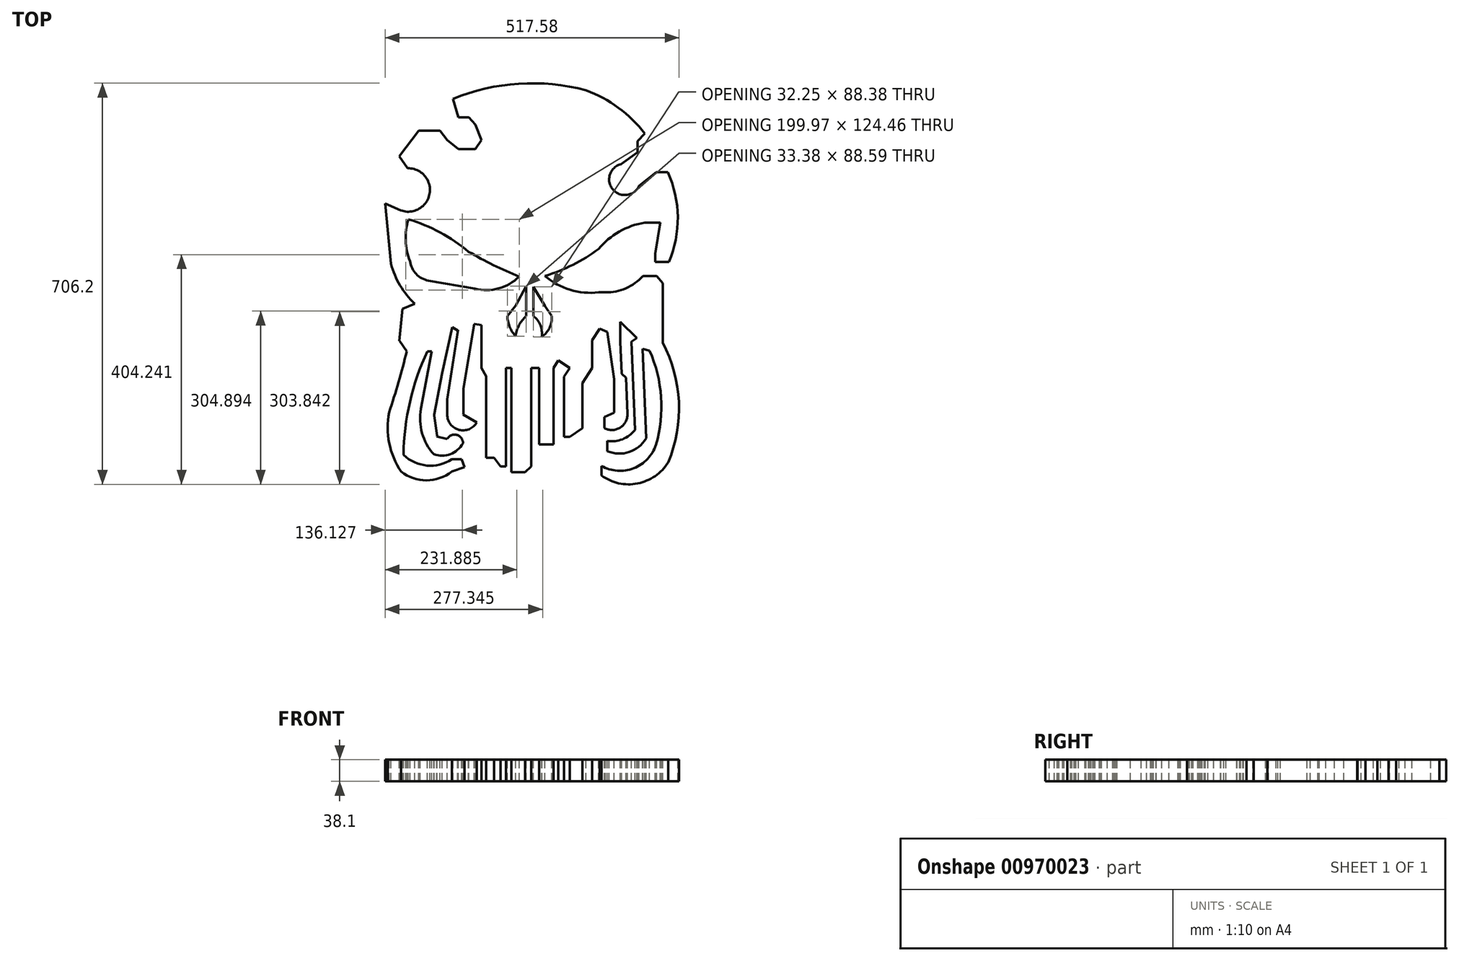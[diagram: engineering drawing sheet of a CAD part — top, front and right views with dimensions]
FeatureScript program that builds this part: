
annotation { "Feature Type Name" : "Feature", "Feature Type Description" : "" }
export const myFeature = defineFeature(function(context is Context, id is Id, definition is map)
    precondition{}
    {
        {
            var Q0;
            Q0=qCreatedBy(makeId("Top.planeOp"),FACE);
            var sketch = newSketch(context, id + "F0", { "sketchPlane" : qUnion([Q0])});
            skLineSegment(sketch, "E0", {"start": v(-722.51, 11.97) * mm, "end": v(-722.51, -131.34) * mm});
            skLineSegment(sketch, "E1", {"start": v(-722.51, -131.34) * mm, "end": v(-708.67, -131.34) * mm});
            skLineSegment(sketch, "E2", {"start": v(-708.67, -131.34) * mm, "end": v(-697.27, -146.82) * mm});
            skLineSegment(sketch, "E3", {"start": v(-697.27, -146.82) * mm, "end": v(-687.81, -146.82) * mm});
            skLineSegment(sketch, "E4", {"start": v(-687.81, -146.82) * mm, "end": v(-687.81, 12.03) * mm});
            skLineSegment(sketch, "E5", {"start": v(-687.81, 12.03) * mm, "end": v(-687.81, 26.51) * mm});
            skLineSegment(sketch, "E6", {"start": v(-687.81, 26.51) * mm, "end": v(-678.37, 26.51) * mm});
            skLineSegment(sketch, "E7", {"start": v(-678.37, 26.51) * mm, "end": v(-678.37, -157.24) * mm});
            skLineSegment(sketch, "E8", {"start": v(-678.37, -157.24) * mm, "end": v(-653.98, -157.24) * mm});
            skLineSegment(sketch, "E9", {"start": v(-653.98, -157.24) * mm, "end": v(-643.31, -146.82) * mm});
            skLineSegment(sketch, "E10", {"start": v(-643.31, -146.82) * mm, "end": v(-643.31, 26.51) * mm});
            skLineSegment(sketch, "E11", {"start": v(-643.31, 26.51) * mm, "end": v(-629.14, 26.51) * mm});
            skLineSegment(sketch, "E12", {"start": v(-629.14, 26.51) * mm, "end": v(-629.14, -107.97) * mm});
            skLineSegment(sketch, "E13", {"start": v(-629.14, -107.97) * mm, "end": v(-618.05, -107.97) * mm});
            skLineSegment(sketch, "E14", {"start": v(-618.05, -107.97) * mm, "end": v(-604.25, -107.97) * mm});
            skLineSegment(sketch, "E15", {"start": v(-604.25, -107.97) * mm, "end": v(-604.25, 26.51) * mm});
            skLineSegment(sketch, "E16", {"start": v(-604.25, 26.51) * mm, "end": v(-595.66, 39.65) * mm});
            skLineSegment(sketch, "E17", {"start": v(-595.66, 39.65) * mm, "end": v(-575.55, 26.51) * mm});
            skLineSegment(sketch, "E18", {"start": v(-575.55, 26.51) * mm, "end": v(-585.6, 11.12) * mm});
            skLineSegment(sketch, "E19", {"start": v(-585.6, 11.12) * mm, "end": v(-585.6, -94.7) * mm});
            skLineSegment(sketch, "E20", {"start": v(-585.6, -94.7) * mm, "end": v(-575.55, -94.7) * mm});
            skLineSegment(sketch, "E21", {"start": v(-575.55, -94.7) * mm, "end": v(-553.4, -79.77) * mm});
            skLineSegment(sketch, "E22", {"start": v(-553.4, -79.77) * mm, "end": v(-553.4, 0) * mm});
            skLineSegment(sketch, "E23", {"start": v(-553.4, 0) * mm, "end": v(-536.08, 26.51) * mm});
            skLineSegment(sketch, "E24", {"start": v(-536.08, 26.51) * mm, "end": v(-536.08, 75.42) * mm});
            skLineSegment(sketch, "E25", {"start": v(-536.08, 75.42) * mm, "end": v(-522.9, 95.58) * mm});
            skArc(sketch, "E26", {"start": v(-546.97, 515.55) * mm, "mid": v(-665.37, 527.1) * mm, "end": v(-781.28, 500.3) * mm});
            skArc(sketch, "E27", {"start": v(-890.2, 209.79) * mm, "mid": v(-874.31, 171.83) * mm, "end": v(-848.63, 139.69) * mm});
            skLineSegment(sketch, "E28", {"start": v(-890.2, 209.79) * mm, "end": v(-900.6, 315.97) * mm});
            skArc(sketch, "E29", {"start": v(-873.07, 303.95) * mm, "mid": v(-822.23, 333.84) * mm, "end": v(-861.1, 378.2) * mm});
            skLineSegment(sketch, "E30", {"start": v(-873.07, 303.95) * mm, "end": v(-900.6, 315.97) * mm});
            skLineSegment(sketch, "E31", {"start": v(-861.1, 378.2) * mm, "end": v(-876, 399.5) * mm});
            skLineSegment(sketch, "E32", {"start": v(-876, 399.5) * mm, "end": v(-841.26, 444.55) * mm});
            skLineSegment(sketch, "E33", {"start": v(-841.26, 444.55) * mm, "end": v(-804.24, 444.55) * mm});
            skLineSegment(sketch, "E34", {"start": v(-804.24, 444.55) * mm, "end": v(-791.29, 428) * mm});
            skLineSegment(sketch, "E35", {"start": v(-791.29, 428) * mm, "end": v(-771.63, 412.14) * mm});
            skLineSegment(sketch, "E36", {"start": v(-771.63, 412.14) * mm, "end": v(-742.1, 412.14) * mm});
            skLineSegment(sketch, "E37", {"start": v(-742.1, 412.14) * mm, "end": v(-731.04, 428) * mm});
            skLineSegment(sketch, "E38", {"start": v(-731.04, 428) * mm, "end": v(-742.1, 455.33) * mm});
            skLineSegment(sketch, "E39", {"start": v(-742.1, 455.33) * mm, "end": v(-753.4, 467.53) * mm});
            skLineSegment(sketch, "E40", {"start": v(-753.4, 467.53) * mm, "end": v(-771.63, 467.53) * mm});
            skLineSegment(sketch, "E41", {"start": v(-771.63, 467.53) * mm, "end": v(-781.28, 500.3) * mm});
            skArc(sketch, "E42", {"start": v(-443.19, 439.34) * mm, "mid": v(-489.8, 484.64) * mm, "end": v(-546.97, 515.55) * mm});
            skLineSegment(sketch, "E43", {"start": v(-443.19, 439.34) * mm, "end": v(-455.81, 426.16) * mm});
            skLineSegment(sketch, "E44", {"start": v(-455.81, 426.16) * mm, "end": v(-455.81, 406.54) * mm});
            skLineSegment(sketch, "E45", {"start": v(-455.81, 406.54) * mm, "end": v(-485.44, 385.35) * mm});
            skArc(sketch, "E46", {"start": v(-485.44, 385.35) * mm, "mid": v(-499.49, 340.79) * mm, "end": v(-453.23, 347.45) * mm});
            skLineSegment(sketch, "E47", {"start": v(-453.23, 347.45) * mm, "end": v(-423.25, 371.41) * mm});
            skLineSegment(sketch, "E48", {"start": v(-423.25, 371.41) * mm, "end": v(-402.75, 371.1) * mm});
            skArc(sketch, "E49", {"start": v(-400.77, 213.04) * mm, "mid": v(-385.19, 292.28) * mm, "end": v(-402.75, 371.1) * mm});
            skLineSegment(sketch, "E50", {"start": v(-400.77, 213.04) * mm, "end": v(-424.77, 213.04) * mm});
            skLineSegment(sketch, "E51", {"start": v(-424.77, 213.04) * mm, "end": v(-424.77, 227.84) * mm});
            skLineSegment(sketch, "E52", {"start": v(-424.77, 227.84) * mm, "end": v(-415.97, 282.48) * mm});
            skArc(sketch, "E53", {"start": v(-443.19, 282.48) * mm, "mid": v(-488.23, 266.6) * mm, "end": v(-524.75, 235.83) * mm});
            skLineSegment(sketch, "E54", {"start": v(-443.19, 282.48) * mm, "end": v(-415.97, 282.48) * mm});
            skArc(sketch, "E55", {"start": v(-618.96, 188.64) * mm, "mid": v(-569.87, 208.28) * mm, "end": v(-524.75, 235.83) * mm});
            skArc(sketch, "E56", {"start": v(-618.96, 188.64) * mm, "mid": v(-574.9, 164.26) * mm, "end": v(-524.75, 159.64) * mm});
            skArc(sketch, "E57", {"start": v(-512.7, 159.64) * mm, "mid": v(-476.43, 166.9) * mm, "end": v(-446.5, 188.64) * mm});
            skLineSegment(sketch, "E58", {"start": v(-512.7, 159.64) * mm, "end": v(-524.75, 159.64) * mm});
            skLineSegment(sketch, "E59", {"start": v(-446.5, 188.64) * mm, "end": v(-422.22, 188.64) * mm});
            skLineSegment(sketch, "E60", {"start": v(-422.22, 188.64) * mm, "end": v(-411.7, 176) * mm});
            skLineSegment(sketch, "E61", {"start": v(-411.7, 176) * mm, "end": v(-411.7, 128.35) * mm});
            skLineSegment(sketch, "E62", {"start": v(-411.7, 128.35) * mm, "end": v(-411.7, 104.7) * mm});
            skLineSegment(sketch, "E63", {"start": v(-411.7, 104.7) * mm, "end": v(-411.7, 71.28) * mm});
            skArc(sketch, "E64", {"start": v(-402.15, -139.77) * mm, "mid": v(-383.27, -33.18) * mm, "end": v(-411.7, 71.28) * mm});
            skArc(sketch, "E65", {"start": v(-519.79, -162.6) * mm, "mid": v(-455.99, -176.83) * mm, "end": v(-402.15, -139.77) * mm});
            skLineSegment(sketch, "E66", {"start": v(-519.79, -162.6) * mm, "end": v(-519.79, -145.96) * mm});
            skArc(sketch, "E67", {"start": v(-519.79, -145.96) * mm, "mid": v(-462.8, -149.95) * mm, "end": v(-423.38, -108.6) * mm});
            skArc(sketch, "E68", {"start": v(-423.38, -108.6) * mm, "mid": v(-414.63, -24.65) * mm, "end": v(-434.9, 57.3) * mm});
            skLineSegment(sketch, "E69", {"start": v(-434.9, 57.3) * mm, "end": v(-446.95, 59.87) * mm});
            skLineSegment(sketch, "E70", {"start": v(-446.95, 59.87) * mm, "end": v(-440.92, -97.48) * mm});
            skArc(sketch, "E71", {"start": v(-509.45, -119.95) * mm, "mid": v(-471, -121.5) * mm, "end": v(-440.92, -97.48) * mm});
            skLineSegment(sketch, "E72", {"start": v(-509.45, -119.95) * mm, "end": v(-509.45, -101.64) * mm});
            skArc(sketch, "E73", {"start": v(-509.45, -101.64) * mm, "mid": v(-482.36, -98.94) * mm, "end": v(-460.6, -82.56) * mm});
            skLineSegment(sketch, "E74", {"start": v(-460.6, -82.56) * mm, "end": v(-465.43, 43.16) * mm});
            skLineSegment(sketch, "E75", {"start": v(-465.43, 43.16) * mm, "end": v(-466.57, 73.07) * mm});
            skLineSegment(sketch, "E76", {"start": v(-466.57, 73.07) * mm, "end": v(-457.03, 79.51) * mm});
            skLineSegment(sketch, "E77", {"start": v(-457.03, 79.51) * mm, "end": v(-486.17, 107.8) * mm});
            skLineSegment(sketch, "E78", {"start": v(-486.17, 107.8) * mm, "end": v(-486.17, 73.07) * mm});
            skLineSegment(sketch, "E79", {"start": v(-486.17, 73.07) * mm, "end": v(-484, 16.62) * mm});
            skLineSegment(sketch, "E80", {"start": v(-484, 16.62) * mm, "end": v(-476.28, 9.12) * mm});
            skLineSegment(sketch, "E81", {"start": v(-476.28, 9.12) * mm, "end": v(-473.85, -54.4) * mm});
            skArc(sketch, "E82", {"start": v(-514.6, -79.12) * mm, "mid": v(-486.95, -78.75) * mm, "end": v(-473.85, -54.4) * mm});
            skLineSegment(sketch, "E83", {"start": v(-514.6, -79.12) * mm, "end": v(-514.6, -59.9) * mm});
            skLineSegment(sketch, "E84", {"start": v(-514.6, -59.9) * mm, "end": v(-497.3, -51.94) * mm});
            skLineSegment(sketch, "E85", {"start": v(-497.3, -51.94) * mm, "end": v(-497.3, 6.84) * mm});
            skLineSegment(sketch, "E86", {"start": v(-497.3, 6.84) * mm, "end": v(-509.28, 89.94) * mm});
            skLineSegment(sketch, "E87", {"start": v(-509.28, 89.94) * mm, "end": v(-522.9, 95.58) * mm});
            skLineSegment(sketch, "E88", {"start": v(-848.63, 139.69) * mm, "end": v(-870.35, 130.46) * mm});
            skLineSegment(sketch, "E89", {"start": v(-869.76, 130.65) * mm, "end": v(-875.8, 73.95) * mm});
            skLineSegment(sketch, "E90", {"start": v(-875.2, 74.14) * mm, "end": v(-862.71, 55.63) * mm});
            skArc(sketch, "E91", {"start": v(-893.6, -51.72) * mm, "mid": v(-876.96, 1.61) * mm, "end": v(-862.71, 55.63) * mm});
            skArc(sketch, "E92", {"start": v(-893.6, -51.72) * mm, "mid": v(-893.43, -105.84) * mm, "end": v(-872.76, -155.86) * mm});
            skArc(sketch, "E93", {"start": v(-872.76, -155.86) * mm, "mid": v(-827.97, -171.32) * mm, "end": v(-783.18, -155.86) * mm});
            skLineSegment(sketch, "E94", {"start": v(-783.18, -155.86) * mm, "end": v(-760.91, -148) * mm});
            skLineSegment(sketch, "E95", {"start": v(-760.91, -148) * mm, "end": v(-765.86, -133.98) * mm});
            skLineSegment(sketch, "E96", {"start": v(-765.86, -133.98) * mm, "end": v(-783.18, -133.98) * mm});
            skArc(sketch, "E97", {"start": v(-868.16, -126.35) * mm, "mid": v(-827.02, -145.27) * mm, "end": v(-783.18, -133.98) * mm});
            skArc(sketch, "E98", {"start": v(-826.02, 56.02) * mm, "mid": v(-856.96, -32.88) * mm, "end": v(-868.16, -126.35) * mm});
            skLineSegment(sketch, "E99", {"start": v(-826.02, 56.02) * mm, "end": v(-818.54, 56.02) * mm});
            skLineSegment(sketch, "E100", {"start": v(-818.54, 56.02) * mm, "end": v(-837.47, -45.44) * mm});
            skArc(sketch, "E101", {"start": v(-837.47, -45.44) * mm, "mid": v(-835.52, -88.14) * mm, "end": v(-814.8, -125.52) * mm});
            skArc(sketch, "E102", {"start": v(-814.8, -125.52) * mm, "mid": v(-785.8, -125.13) * mm, "end": v(-763.58, -106.47) * mm});
            skArc(sketch, "E103", {"start": v(-763.58, -106.47) * mm, "mid": v(-774.3, -91.33) * mm, "end": v(-791.32, -98.73) * mm});
            skLineSegment(sketch, "E104", {"start": v(-791.32, -98.73) * mm, "end": v(-809.62, -93.87) * mm});
            skLineSegment(sketch, "E105", {"start": v(-809.22, -93.09) * mm, "end": v(-814.46, -57.61) * mm});
            skLineSegment(sketch, "E106", {"start": v(-814.46, -55.65) * mm, "end": v(-800.12, 17.4) * mm});
            skLineSegment(sketch, "E107", {"start": v(-800.12, 17.4) * mm, "end": v(-782.42, 98.05) * mm});
            skLineSegment(sketch, "E108", {"start": v(-782.42, 98.05) * mm, "end": v(-772.88, 92.6) * mm});
            skLineSegment(sketch, "E109", {"start": v(-772.39, 93.45) * mm, "end": v(-791.32, -28.64) * mm});
            skLineSegment(sketch, "E110", {"start": v(-791.32, -28.64) * mm, "end": v(-791.32, -55.45) * mm});
            skArc(sketch, "E111", {"start": v(-791.32, -55.45) * mm, "mid": v(-770.63, -82.39) * mm, "end": v(-739.28, -69.33) * mm});
            skLineSegment(sketch, "E112", {"start": v(-739.28, -69.33) * mm, "end": v(-763.45, -55.45) * mm});
            skLineSegment(sketch, "E113", {"start": v(-762.67, -54.03) * mm, "end": v(-762.67, -9.41) * mm});
            skLineSegment(sketch, "E114", {"start": v(-762.67, -9.41) * mm, "end": v(-743.82, 103.92) * mm});
            skLineSegment(sketch, "E115", {"start": v(-743.02, 103.92) * mm, "end": v(-731.2, 101.96) * mm});
            skLineSegment(sketch, "E116", {"start": v(-731.2, 101.96) * mm, "end": v(-731.2, 26.49) * mm});
            skLineSegment(sketch, "E117", {"start": v(-731.2, 26.49) * mm, "end": v(-722.51, 11.97) * mm});
            skLineSegment(sketch, "E118", {"start": v(-762.67, -54.03) * mm, "end": v(-763.45, -55.45) * mm});
            skLineSegment(sketch, "E119", {"start": v(-772.88, 92.6) * mm, "end": v(-772.39, 93.45) * mm});
            skLineSegment(sketch, "E120", {"start": v(-875.8, 73.95) * mm, "end": v(-875.2, 74.14) * mm});
            skLineSegment(sketch, "E121", {"start": v(-870.35, 130.46) * mm, "end": v(-869.76, 130.65) * mm});
            skLineSegment(sketch, "E122", {"start": v(-814.46, -55.65) * mm, "end": v(-814.46, -57.61) * mm});
            skLineSegment(sketch, "E123", {"start": v(-809.22, -93.09) * mm, "end": v(-809.62, -93.87) * mm});
            skLineSegment(sketch, "E124", {"start": v(-743.82, 103.92) * mm, "end": v(-743.02, 103.92) * mm});
            skSolve(sketch);
        }
        {
            var Q0;
            Q0 = qSketchRegion(id + "F0", true);
            extrude(context, id + "F1", {"entities" : qUnion([Q0]), "oppositeDirection" : true, "depth" : 38.1 * mm, "offsetDistance" : 25.4 * mm});
        }
        {
            var Q0;
            Q0=qCreatedBy(makeId("Top.planeOp"),FACE);
            var sketch = newSketch(context, id + "F2", { "sketchPlane" : qUnion([Q0])});
            skArc(sketch, "E125", {"start": v(-753.6, 231.31) * mm, "mid": v(-803.7, 265.25) * mm, "end": v(-859.7, 288.15) * mm});
            skArc(sketch, "E126", {"start": v(-753.6, 231.31) * mm, "mid": v(-709.86, 207.7) * mm, "end": v(-664.49, 187.38) * mm});
            skArc(sketch, "E127", {"start": v(-742.39, 166.04) * mm, "mid": v(-700.68, 166.65) * mm, "end": v(-664.49, 187.38) * mm});
            skLineSegment(sketch, "E128", {"start": v(-742.39, 166.04) * mm, "end": v(-824.03, 180.25) * mm});
            skArc(sketch, "E129", {"start": v(-856.63, 214.6) * mm, "mid": v(-846.02, 192.03) * mm, "end": v(-824.03, 180.25) * mm});
            skArc(sketch, "E130", {"start": v(-859.7, 288.15) * mm, "mid": v(-864.46, 251.12) * mm, "end": v(-856.63, 214.6) * mm});
            skLineSegment(sketch, "E131", {"start": v(-652.47, 170.87) * mm, "end": v(-670.86, 136.11) * mm});
            skLineSegment(sketch, "E132", {"start": v(-670.86, 136.11) * mm, "end": v(-685.4, 117.95) * mm});
            skArc(sketch, "E133", {"start": v(-685.4, 117.95) * mm, "mid": v(-681.12, 98.9) * mm, "end": v(-670.89, 82.28) * mm});
            skArc(sketch, "E134", {"start": v(-652.02, 117.95) * mm, "mid": v(-664.67, 101.81) * mm, "end": v(-670.89, 82.28) * mm});
            skLineSegment(sketch, "E135", {"start": v(-652.47, 170.87) * mm, "end": v(-652.02, 117.95) * mm});
            skLineSegment(sketch, "E136", {"start": v(-639.38, 169.7) * mm, "end": v(-639.38, 117.95) * mm});
            skArc(sketch, "E137", {"start": v(-624.94, 81.33) * mm, "mid": v(-627.12, 101.63) * mm, "end": v(-639.38, 117.95) * mm});
            skArc(sketch, "E138", {"start": v(-624.94, 81.33) * mm, "mid": v(-611.15, 97.26) * mm, "end": v(-607.16, 117.95) * mm});
            skLineSegment(sketch, "E139", {"start": v(-639.38, 169.7) * mm, "end": v(-619.27, 135.97) * mm});
            skLineSegment(sketch, "E140", {"start": v(-619.27, 135.97) * mm, "end": v(-607.16, 117.95) * mm});
            skSolve(sketch);
        }
        {
            var Q0;
            Q0 = qSketchRegion(id + "F2", true);
            extrude(context, id + "F3", {"entities" : qUnion([Q0]), "oppositeDirection" : true, "depth" : 127 * mm, "offsetDistance" : 25.4 * mm});
        }
        {
            var Q0;
            Q0=makeQuery(id+"F3.opExtrude","SWEPT_BODY",BODY,{"disambiguationData":[OSD([sQuery(id+"F2.wireOp",EDGE,"E125"),sQuery(id+"F2.wireOp",EDGE,"E126"),sQuery(id+"F2.wireOp",EDGE,"E127"),sQuery(id+"F2.wireOp",EDGE,"E128"),sQuery(id+"F2.wireOp",EDGE,"E129"),sQuery(id+"F2.wireOp",EDGE,"E130")])]});
            var Q1;
            Q1=makeQuery(id+"F1.opExtrude","SWEPT_BODY",BODY,{"disambiguationData":[OSD([sQuery(id+"F0.wireOp",EDGE,"E0"),sQuery(id+"F0.wireOp",EDGE,"E1"),sQuery(id+"F0.wireOp",EDGE,"E2"),sQuery(id+"F0.wireOp",EDGE,"E3"),sQuery(id+"F0.wireOp",EDGE,"E4"),sQuery(id+"F0.wireOp",EDGE,"E5"),sQuery(id+"F0.wireOp",EDGE,"E6"),sQuery(id+"F0.wireOp",EDGE,"E7"),sQuery(id+"F0.wireOp",EDGE,"E8"),sQuery(id+"F0.wireOp",EDGE,"E9"),sQuery(id+"F0.wireOp",EDGE,"E10"),sQuery(id+"F0.wireOp",EDGE,"E11"),sQuery(id+"F0.wireOp",EDGE,"E12"),sQuery(id+"F0.wireOp",EDGE,"E13"),sQuery(id+"F0.wireOp",EDGE,"E14"),sQuery(id+"F0.wireOp",EDGE,"E15"),sQuery(id+"F0.wireOp",EDGE,"E16"),sQuery(id+"F0.wireOp",EDGE,"E17"),sQuery(id+"F0.wireOp",EDGE,"E18"),sQuery(id+"F0.wireOp",EDGE,"E19"),sQuery(id+"F0.wireOp",EDGE,"E20"),sQuery(id+"F0.wireOp",EDGE,"E21"),sQuery(id+"F0.wireOp",EDGE,"E22"),sQuery(id+"F0.wireOp",EDGE,"E23"),sQuery(id+"F0.wireOp",EDGE,"E24"),sQuery(id+"F0.wireOp",EDGE,"E25"),sQuery(id+"F0.wireOp",EDGE,"E26"),sQuery(id+"F0.wireOp",EDGE,"E27"),sQuery(id+"F0.wireOp",EDGE,"E28"),sQuery(id+"F0.wireOp",EDGE,"E29"),sQuery(id+"F0.wireOp",EDGE,"E30"),sQuery(id+"F0.wireOp",EDGE,"E31"),sQuery(id+"F0.wireOp",EDGE,"E32"),sQuery(id+"F0.wireOp",EDGE,"E33"),sQuery(id+"F0.wireOp",EDGE,"E34"),sQuery(id+"F0.wireOp",EDGE,"E35"),sQuery(id+"F0.wireOp",EDGE,"E36"),sQuery(id+"F0.wireOp",EDGE,"E37"),sQuery(id+"F0.wireOp",EDGE,"E38"),sQuery(id+"F0.wireOp",EDGE,"E39"),sQuery(id+"F0.wireOp",EDGE,"E40"),sQuery(id+"F0.wireOp",EDGE,"E41"),sQuery(id+"F0.wireOp",EDGE,"E42"),sQuery(id+"F0.wireOp",EDGE,"E43"),sQuery(id+"F0.wireOp",EDGE,"E44"),sQuery(id+"F0.wireOp",EDGE,"E45"),sQuery(id+"F0.wireOp",EDGE,"E46"),sQuery(id+"F0.wireOp",EDGE,"E47"),sQuery(id+"F0.wireOp",EDGE,"E48"),sQuery(id+"F0.wireOp",EDGE,"E49"),sQuery(id+"F0.wireOp",EDGE,"E50"),sQuery(id+"F0.wireOp",EDGE,"E51"),sQuery(id+"F0.wireOp",EDGE,"E52"),sQuery(id+"F0.wireOp",EDGE,"E53"),sQuery(id+"F0.wireOp",EDGE,"E54"),sQuery(id+"F0.wireOp",EDGE,"E55"),sQuery(id+"F0.wireOp",EDGE,"E56"),sQuery(id+"F0.wireOp",EDGE,"E57"),sQuery(id+"F0.wireOp",EDGE,"E58"),sQuery(id+"F0.wireOp",EDGE,"E59"),sQuery(id+"F0.wireOp",EDGE,"E60"),sQuery(id+"F0.wireOp",EDGE,"E61"),sQuery(id+"F0.wireOp",EDGE,"E62"),sQuery(id+"F0.wireOp",EDGE,"E63"),sQuery(id+"F0.wireOp",EDGE,"E64"),sQuery(id+"F0.wireOp",EDGE,"E65"),sQuery(id+"F0.wireOp",EDGE,"E66"),sQuery(id+"F0.wireOp",EDGE,"E67"),sQuery(id+"F0.wireOp",EDGE,"E68"),sQuery(id+"F0.wireOp",EDGE,"E69"),sQuery(id+"F0.wireOp",EDGE,"E70"),sQuery(id+"F0.wireOp",EDGE,"E71"),sQuery(id+"F0.wireOp",EDGE,"E72"),sQuery(id+"F0.wireOp",EDGE,"E73"),sQuery(id+"F0.wireOp",EDGE,"E74"),sQuery(id+"F0.wireOp",EDGE,"E75"),sQuery(id+"F0.wireOp",EDGE,"E76"),sQuery(id+"F0.wireOp",EDGE,"E77"),sQuery(id+"F0.wireOp",EDGE,"E78"),sQuery(id+"F0.wireOp",EDGE,"E79"),sQuery(id+"F0.wireOp",EDGE,"E80"),sQuery(id+"F0.wireOp",EDGE,"E81"),sQuery(id+"F0.wireOp",EDGE,"E82"),sQuery(id+"F0.wireOp",EDGE,"E83"),sQuery(id+"F0.wireOp",EDGE,"E84"),sQuery(id+"F0.wireOp",EDGE,"E85"),sQuery(id+"F0.wireOp",EDGE,"E86"),sQuery(id+"F0.wireOp",EDGE,"E87"),sQuery(id+"F0.wireOp",EDGE,"E88"),sQuery(id+"F0.wireOp",EDGE,"E89"),sQuery(id+"F0.wireOp",EDGE,"E90"),sQuery(id+"F0.wireOp",EDGE,"E91"),sQuery(id+"F0.wireOp",EDGE,"E92"),sQuery(id+"F0.wireOp",EDGE,"E93"),sQuery(id+"F0.wireOp",EDGE,"E94"),sQuery(id+"F0.wireOp",EDGE,"E95"),sQuery(id+"F0.wireOp",EDGE,"E96"),sQuery(id+"F0.wireOp",EDGE,"E97"),sQuery(id+"F0.wireOp",EDGE,"E98"),sQuery(id+"F0.wireOp",EDGE,"E99"),sQuery(id+"F0.wireOp",EDGE,"E100"),sQuery(id+"F0.wireOp",EDGE,"E101"),sQuery(id+"F0.wireOp",EDGE,"E102"),sQuery(id+"F0.wireOp",EDGE,"E103"),sQuery(id+"F0.wireOp",EDGE,"E104"),sQuery(id+"F0.wireOp",EDGE,"E105"),sQuery(id+"F0.wireOp",EDGE,"E106"),sQuery(id+"F0.wireOp",EDGE,"E107"),sQuery(id+"F0.wireOp",EDGE,"E108"),sQuery(id+"F0.wireOp",EDGE,"E109"),sQuery(id+"F0.wireOp",EDGE,"E110"),sQuery(id+"F0.wireOp",EDGE,"E111"),sQuery(id+"F0.wireOp",EDGE,"E112"),sQuery(id+"F0.wireOp",EDGE,"E113"),sQuery(id+"F0.wireOp",EDGE,"E114"),sQuery(id+"F0.wireOp",EDGE,"E115"),sQuery(id+"F0.wireOp",EDGE,"E116"),sQuery(id+"F0.wireOp",EDGE,"E117"),sQuery(id+"F0.wireOp",EDGE,"E118"),sQuery(id+"F0.wireOp",EDGE,"E119"),sQuery(id+"F0.wireOp",EDGE,"E120"),sQuery(id+"F0.wireOp",EDGE,"E121"),sQuery(id+"F0.wireOp",EDGE,"E122"),sQuery(id+"F0.wireOp",EDGE,"E123"),sQuery(id+"F0.wireOp",EDGE,"E124")])]});
            booleanBodies(context, id + "F4", {"operationType" : BooleanOperationType.SUBTRACTION, "tools" : qUnion([Q0]), "targets" : qUnion([Q1])});
        }
        {
            var Q0;
            Q0=makeQuery(id+"F3.opExtrude","SWEPT_BODY",BODY,{"disambiguationData":[OSD([sQuery(id+"F2.wireOp",EDGE,"E136"),sQuery(id+"F2.wireOp",EDGE,"E137"),sQuery(id+"F2.wireOp",EDGE,"E138"),sQuery(id+"F2.wireOp",EDGE,"E139"),sQuery(id+"F2.wireOp",EDGE,"E140")])]});
            var Q1;
            Q1=makeQuery(id+"F1.opExtrude","SWEPT_BODY",BODY,{"disambiguationData":[OSD([sQuery(id+"F0.wireOp",EDGE,"E0"),sQuery(id+"F0.wireOp",EDGE,"E1"),sQuery(id+"F0.wireOp",EDGE,"E2"),sQuery(id+"F0.wireOp",EDGE,"E3"),sQuery(id+"F0.wireOp",EDGE,"E4"),sQuery(id+"F0.wireOp",EDGE,"E5"),sQuery(id+"F0.wireOp",EDGE,"E6"),sQuery(id+"F0.wireOp",EDGE,"E7"),sQuery(id+"F0.wireOp",EDGE,"E8"),sQuery(id+"F0.wireOp",EDGE,"E9"),sQuery(id+"F0.wireOp",EDGE,"E10"),sQuery(id+"F0.wireOp",EDGE,"E11"),sQuery(id+"F0.wireOp",EDGE,"E12"),sQuery(id+"F0.wireOp",EDGE,"E13"),sQuery(id+"F0.wireOp",EDGE,"E14"),sQuery(id+"F0.wireOp",EDGE,"E15"),sQuery(id+"F0.wireOp",EDGE,"E16"),sQuery(id+"F0.wireOp",EDGE,"E17"),sQuery(id+"F0.wireOp",EDGE,"E18"),sQuery(id+"F0.wireOp",EDGE,"E19"),sQuery(id+"F0.wireOp",EDGE,"E20"),sQuery(id+"F0.wireOp",EDGE,"E21"),sQuery(id+"F0.wireOp",EDGE,"E22"),sQuery(id+"F0.wireOp",EDGE,"E23"),sQuery(id+"F0.wireOp",EDGE,"E24"),sQuery(id+"F0.wireOp",EDGE,"E25"),sQuery(id+"F0.wireOp",EDGE,"E26"),sQuery(id+"F0.wireOp",EDGE,"E27"),sQuery(id+"F0.wireOp",EDGE,"E28"),sQuery(id+"F0.wireOp",EDGE,"E29"),sQuery(id+"F0.wireOp",EDGE,"E30"),sQuery(id+"F0.wireOp",EDGE,"E31"),sQuery(id+"F0.wireOp",EDGE,"E32"),sQuery(id+"F0.wireOp",EDGE,"E33"),sQuery(id+"F0.wireOp",EDGE,"E34"),sQuery(id+"F0.wireOp",EDGE,"E35"),sQuery(id+"F0.wireOp",EDGE,"E36"),sQuery(id+"F0.wireOp",EDGE,"E37"),sQuery(id+"F0.wireOp",EDGE,"E38"),sQuery(id+"F0.wireOp",EDGE,"E39"),sQuery(id+"F0.wireOp",EDGE,"E40"),sQuery(id+"F0.wireOp",EDGE,"E41"),sQuery(id+"F0.wireOp",EDGE,"E42"),sQuery(id+"F0.wireOp",EDGE,"E43"),sQuery(id+"F0.wireOp",EDGE,"E44"),sQuery(id+"F0.wireOp",EDGE,"E45"),sQuery(id+"F0.wireOp",EDGE,"E46"),sQuery(id+"F0.wireOp",EDGE,"E47"),sQuery(id+"F0.wireOp",EDGE,"E48"),sQuery(id+"F0.wireOp",EDGE,"E49"),sQuery(id+"F0.wireOp",EDGE,"E50"),sQuery(id+"F0.wireOp",EDGE,"E51"),sQuery(id+"F0.wireOp",EDGE,"E52"),sQuery(id+"F0.wireOp",EDGE,"E53"),sQuery(id+"F0.wireOp",EDGE,"E54"),sQuery(id+"F0.wireOp",EDGE,"E55"),sQuery(id+"F0.wireOp",EDGE,"E56"),sQuery(id+"F0.wireOp",EDGE,"E57"),sQuery(id+"F0.wireOp",EDGE,"E58"),sQuery(id+"F0.wireOp",EDGE,"E59"),sQuery(id+"F0.wireOp",EDGE,"E60"),sQuery(id+"F0.wireOp",EDGE,"E61"),sQuery(id+"F0.wireOp",EDGE,"E62"),sQuery(id+"F0.wireOp",EDGE,"E63"),sQuery(id+"F0.wireOp",EDGE,"E64"),sQuery(id+"F0.wireOp",EDGE,"E65"),sQuery(id+"F0.wireOp",EDGE,"E66"),sQuery(id+"F0.wireOp",EDGE,"E67"),sQuery(id+"F0.wireOp",EDGE,"E68"),sQuery(id+"F0.wireOp",EDGE,"E69"),sQuery(id+"F0.wireOp",EDGE,"E70"),sQuery(id+"F0.wireOp",EDGE,"E71"),sQuery(id+"F0.wireOp",EDGE,"E72"),sQuery(id+"F0.wireOp",EDGE,"E73"),sQuery(id+"F0.wireOp",EDGE,"E74"),sQuery(id+"F0.wireOp",EDGE,"E75"),sQuery(id+"F0.wireOp",EDGE,"E76"),sQuery(id+"F0.wireOp",EDGE,"E77"),sQuery(id+"F0.wireOp",EDGE,"E78"),sQuery(id+"F0.wireOp",EDGE,"E79"),sQuery(id+"F0.wireOp",EDGE,"E80"),sQuery(id+"F0.wireOp",EDGE,"E81"),sQuery(id+"F0.wireOp",EDGE,"E82"),sQuery(id+"F0.wireOp",EDGE,"E83"),sQuery(id+"F0.wireOp",EDGE,"E84"),sQuery(id+"F0.wireOp",EDGE,"E85"),sQuery(id+"F0.wireOp",EDGE,"E86"),sQuery(id+"F0.wireOp",EDGE,"E87"),sQuery(id+"F0.wireOp",EDGE,"E88"),sQuery(id+"F0.wireOp",EDGE,"E89"),sQuery(id+"F0.wireOp",EDGE,"E90"),sQuery(id+"F0.wireOp",EDGE,"E91"),sQuery(id+"F0.wireOp",EDGE,"E92"),sQuery(id+"F0.wireOp",EDGE,"E93"),sQuery(id+"F0.wireOp",EDGE,"E94"),sQuery(id+"F0.wireOp",EDGE,"E95"),sQuery(id+"F0.wireOp",EDGE,"E96"),sQuery(id+"F0.wireOp",EDGE,"E97"),sQuery(id+"F0.wireOp",EDGE,"E98"),sQuery(id+"F0.wireOp",EDGE,"E99"),sQuery(id+"F0.wireOp",EDGE,"E100"),sQuery(id+"F0.wireOp",EDGE,"E101"),sQuery(id+"F0.wireOp",EDGE,"E102"),sQuery(id+"F0.wireOp",EDGE,"E103"),sQuery(id+"F0.wireOp",EDGE,"E104"),sQuery(id+"F0.wireOp",EDGE,"E105"),sQuery(id+"F0.wireOp",EDGE,"E106"),sQuery(id+"F0.wireOp",EDGE,"E107"),sQuery(id+"F0.wireOp",EDGE,"E108"),sQuery(id+"F0.wireOp",EDGE,"E109"),sQuery(id+"F0.wireOp",EDGE,"E110"),sQuery(id+"F0.wireOp",EDGE,"E111"),sQuery(id+"F0.wireOp",EDGE,"E112"),sQuery(id+"F0.wireOp",EDGE,"E113"),sQuery(id+"F0.wireOp",EDGE,"E114"),sQuery(id+"F0.wireOp",EDGE,"E115"),sQuery(id+"F0.wireOp",EDGE,"E116"),sQuery(id+"F0.wireOp",EDGE,"E117"),sQuery(id+"F0.wireOp",EDGE,"E118"),sQuery(id+"F0.wireOp",EDGE,"E119"),sQuery(id+"F0.wireOp",EDGE,"E120"),sQuery(id+"F0.wireOp",EDGE,"E121"),sQuery(id+"F0.wireOp",EDGE,"E122"),sQuery(id+"F0.wireOp",EDGE,"E123"),sQuery(id+"F0.wireOp",EDGE,"E124")])]});
            booleanBodies(context, id + "F5", {"operationType" : BooleanOperationType.SUBTRACTION, "tools" : qUnion([Q0]), "targets" : qUnion([Q1])});
        }
        {
            var Q0;
            Q0=makeQuery(id+"F3.opExtrude","SWEPT_BODY",BODY,{"disambiguationData":[OSD([sQuery(id+"F2.wireOp",EDGE,"E131"),sQuery(id+"F2.wireOp",EDGE,"E132"),sQuery(id+"F2.wireOp",EDGE,"E133"),sQuery(id+"F2.wireOp",EDGE,"E134"),sQuery(id+"F2.wireOp",EDGE,"E135")])]});
            var Q1;
            Q1=makeQuery(id+"F1.opExtrude","SWEPT_BODY",BODY,{"disambiguationData":[OSD([sQuery(id+"F0.wireOp",EDGE,"E0"),sQuery(id+"F0.wireOp",EDGE,"E1"),sQuery(id+"F0.wireOp",EDGE,"E2"),sQuery(id+"F0.wireOp",EDGE,"E3"),sQuery(id+"F0.wireOp",EDGE,"E4"),sQuery(id+"F0.wireOp",EDGE,"E5"),sQuery(id+"F0.wireOp",EDGE,"E6"),sQuery(id+"F0.wireOp",EDGE,"E7"),sQuery(id+"F0.wireOp",EDGE,"E8"),sQuery(id+"F0.wireOp",EDGE,"E9"),sQuery(id+"F0.wireOp",EDGE,"E10"),sQuery(id+"F0.wireOp",EDGE,"E11"),sQuery(id+"F0.wireOp",EDGE,"E12"),sQuery(id+"F0.wireOp",EDGE,"E13"),sQuery(id+"F0.wireOp",EDGE,"E14"),sQuery(id+"F0.wireOp",EDGE,"E15"),sQuery(id+"F0.wireOp",EDGE,"E16"),sQuery(id+"F0.wireOp",EDGE,"E17"),sQuery(id+"F0.wireOp",EDGE,"E18"),sQuery(id+"F0.wireOp",EDGE,"E19"),sQuery(id+"F0.wireOp",EDGE,"E20"),sQuery(id+"F0.wireOp",EDGE,"E21"),sQuery(id+"F0.wireOp",EDGE,"E22"),sQuery(id+"F0.wireOp",EDGE,"E23"),sQuery(id+"F0.wireOp",EDGE,"E24"),sQuery(id+"F0.wireOp",EDGE,"E25"),sQuery(id+"F0.wireOp",EDGE,"E26"),sQuery(id+"F0.wireOp",EDGE,"E27"),sQuery(id+"F0.wireOp",EDGE,"E28"),sQuery(id+"F0.wireOp",EDGE,"E29"),sQuery(id+"F0.wireOp",EDGE,"E30"),sQuery(id+"F0.wireOp",EDGE,"E31"),sQuery(id+"F0.wireOp",EDGE,"E32"),sQuery(id+"F0.wireOp",EDGE,"E33"),sQuery(id+"F0.wireOp",EDGE,"E34"),sQuery(id+"F0.wireOp",EDGE,"E35"),sQuery(id+"F0.wireOp",EDGE,"E36"),sQuery(id+"F0.wireOp",EDGE,"E37"),sQuery(id+"F0.wireOp",EDGE,"E38"),sQuery(id+"F0.wireOp",EDGE,"E39"),sQuery(id+"F0.wireOp",EDGE,"E40"),sQuery(id+"F0.wireOp",EDGE,"E41"),sQuery(id+"F0.wireOp",EDGE,"E42"),sQuery(id+"F0.wireOp",EDGE,"E43"),sQuery(id+"F0.wireOp",EDGE,"E44"),sQuery(id+"F0.wireOp",EDGE,"E45"),sQuery(id+"F0.wireOp",EDGE,"E46"),sQuery(id+"F0.wireOp",EDGE,"E47"),sQuery(id+"F0.wireOp",EDGE,"E48"),sQuery(id+"F0.wireOp",EDGE,"E49"),sQuery(id+"F0.wireOp",EDGE,"E50"),sQuery(id+"F0.wireOp",EDGE,"E51"),sQuery(id+"F0.wireOp",EDGE,"E52"),sQuery(id+"F0.wireOp",EDGE,"E53"),sQuery(id+"F0.wireOp",EDGE,"E54"),sQuery(id+"F0.wireOp",EDGE,"E55"),sQuery(id+"F0.wireOp",EDGE,"E56"),sQuery(id+"F0.wireOp",EDGE,"E57"),sQuery(id+"F0.wireOp",EDGE,"E58"),sQuery(id+"F0.wireOp",EDGE,"E59"),sQuery(id+"F0.wireOp",EDGE,"E60"),sQuery(id+"F0.wireOp",EDGE,"E61"),sQuery(id+"F0.wireOp",EDGE,"E62"),sQuery(id+"F0.wireOp",EDGE,"E63"),sQuery(id+"F0.wireOp",EDGE,"E64"),sQuery(id+"F0.wireOp",EDGE,"E65"),sQuery(id+"F0.wireOp",EDGE,"E66"),sQuery(id+"F0.wireOp",EDGE,"E67"),sQuery(id+"F0.wireOp",EDGE,"E68"),sQuery(id+"F0.wireOp",EDGE,"E69"),sQuery(id+"F0.wireOp",EDGE,"E70"),sQuery(id+"F0.wireOp",EDGE,"E71"),sQuery(id+"F0.wireOp",EDGE,"E72"),sQuery(id+"F0.wireOp",EDGE,"E73"),sQuery(id+"F0.wireOp",EDGE,"E74"),sQuery(id+"F0.wireOp",EDGE,"E75"),sQuery(id+"F0.wireOp",EDGE,"E76"),sQuery(id+"F0.wireOp",EDGE,"E77"),sQuery(id+"F0.wireOp",EDGE,"E78"),sQuery(id+"F0.wireOp",EDGE,"E79"),sQuery(id+"F0.wireOp",EDGE,"E80"),sQuery(id+"F0.wireOp",EDGE,"E81"),sQuery(id+"F0.wireOp",EDGE,"E82"),sQuery(id+"F0.wireOp",EDGE,"E83"),sQuery(id+"F0.wireOp",EDGE,"E84"),sQuery(id+"F0.wireOp",EDGE,"E85"),sQuery(id+"F0.wireOp",EDGE,"E86"),sQuery(id+"F0.wireOp",EDGE,"E87"),sQuery(id+"F0.wireOp",EDGE,"E88"),sQuery(id+"F0.wireOp",EDGE,"E89"),sQuery(id+"F0.wireOp",EDGE,"E90"),sQuery(id+"F0.wireOp",EDGE,"E91"),sQuery(id+"F0.wireOp",EDGE,"E92"),sQuery(id+"F0.wireOp",EDGE,"E93"),sQuery(id+"F0.wireOp",EDGE,"E94"),sQuery(id+"F0.wireOp",EDGE,"E95"),sQuery(id+"F0.wireOp",EDGE,"E96"),sQuery(id+"F0.wireOp",EDGE,"E97"),sQuery(id+"F0.wireOp",EDGE,"E98"),sQuery(id+"F0.wireOp",EDGE,"E99"),sQuery(id+"F0.wireOp",EDGE,"E100"),sQuery(id+"F0.wireOp",EDGE,"E101"),sQuery(id+"F0.wireOp",EDGE,"E102"),sQuery(id+"F0.wireOp",EDGE,"E103"),sQuery(id+"F0.wireOp",EDGE,"E104"),sQuery(id+"F0.wireOp",EDGE,"E105"),sQuery(id+"F0.wireOp",EDGE,"E106"),sQuery(id+"F0.wireOp",EDGE,"E107"),sQuery(id+"F0.wireOp",EDGE,"E108"),sQuery(id+"F0.wireOp",EDGE,"E109"),sQuery(id+"F0.wireOp",EDGE,"E110"),sQuery(id+"F0.wireOp",EDGE,"E111"),sQuery(id+"F0.wireOp",EDGE,"E112"),sQuery(id+"F0.wireOp",EDGE,"E113"),sQuery(id+"F0.wireOp",EDGE,"E114"),sQuery(id+"F0.wireOp",EDGE,"E115"),sQuery(id+"F0.wireOp",EDGE,"E116"),sQuery(id+"F0.wireOp",EDGE,"E117"),sQuery(id+"F0.wireOp",EDGE,"E118"),sQuery(id+"F0.wireOp",EDGE,"E119"),sQuery(id+"F0.wireOp",EDGE,"E120"),sQuery(id+"F0.wireOp",EDGE,"E121"),sQuery(id+"F0.wireOp",EDGE,"E122"),sQuery(id+"F0.wireOp",EDGE,"E123"),sQuery(id+"F0.wireOp",EDGE,"E124")])]});
            booleanBodies(context, id + "F6", {"operationType" : BooleanOperationType.SUBTRACTION, "tools" : qUnion([Q0]), "targets" : qUnion([Q1])});
        }
    });
